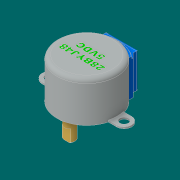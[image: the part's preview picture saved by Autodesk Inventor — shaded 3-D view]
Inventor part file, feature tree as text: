
AUTODESK INVENTOR PART (.ipt)
format: ipt  version: 2016 (Build 200138000, 138)  size: 514,048 bytes
history: native  units: in
note: dims shown in document units (in); Inventor stores cm internally (conversion verified against a paired STEP export)
features: projected_geometry x5, other x1, extrude x1, sketch x1
ambient origin geometry x8: Origin, YZ Plane, XZ Plane, XY Plane, X Axis, Y Axis, Z Axis, Center Point
bodies: Solid1 (feature_tree)
feature tree (8):
  other  "stepperMotor"
  extrude  "Extrusion1"  [1 undecoded]
  sketch  "Sketch1"  dims[d0=0.3937in d1=0.0in]
  projected_geometry  "Projected Loop1"
  projected_geometry  "Projected Loop2"
  projected_geometry  "Projected Loop3"
  projected_geometry  "Projected Loop4"
  projected_geometry  "Projected Loop5"
note: 1 required parameter value undecoded (feature->parameter linkage not recoverable at this tier; creation-order binding heuristic only, values carry confidence <= 0.55)
